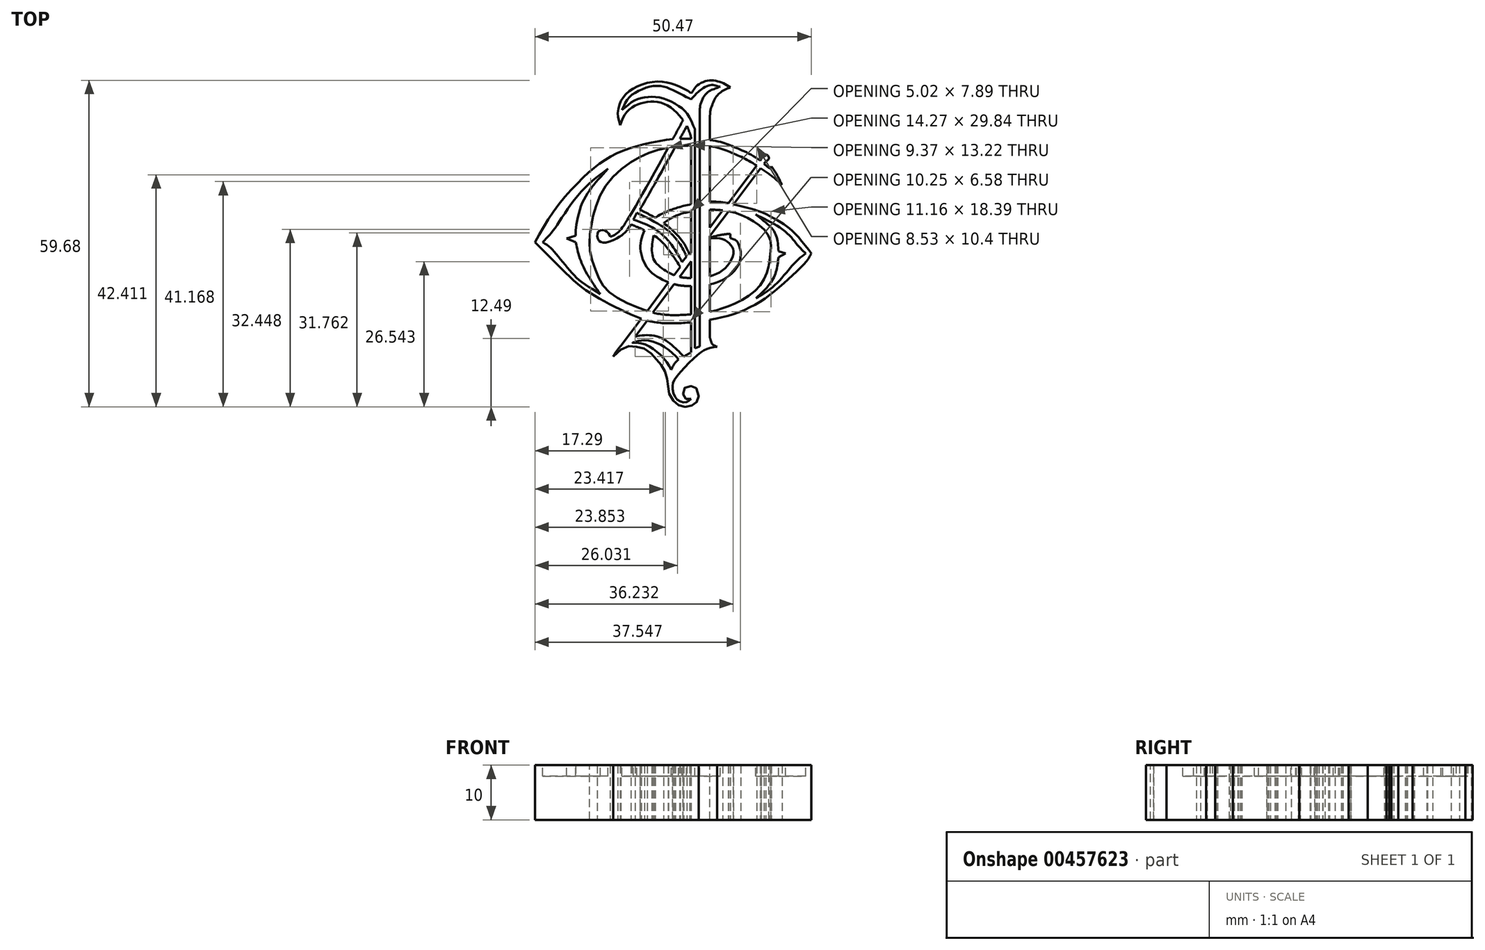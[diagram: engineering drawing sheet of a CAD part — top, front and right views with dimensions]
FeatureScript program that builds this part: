
annotation { "Feature Type Name" : "Feature", "Feature Type Description" : "" }
export const myFeature = defineFeature(function(context is Context, id is Id, definition is map)
    precondition{}
    {
        {
            var Q0;
            Q0=qCreatedBy(makeId("Top.planeOp"),FACE);
            var sketch = newSketch(context, id + "F0", { "sketchPlane" : qUnion([Q0])});
            skFitSpline(sketch, "E0", {"points": [v(7.19, 28.3) * mm, v(5.2, 29.3) * mm, v(2.98, 29.53) * mm, v(0.86, 28.4) * mm, v(0, 27.22) * mm], "startDerivative": vector(-7.6, 5.06) * mm, "endDerivative": vector(-5.78, -5.6) * mm});
            skFitSpline(sketch, "E1", {"points": [v(0, 27.22) * mm, v(-2.3, 28.5) * mm, v(-4.88, 29.3) * mm, v(-8.25, 29.05) * mm, v(-11.21, 27.67) * mm, v(-12.8, 25.88) * mm, v(-13.4, 23.56) * mm, v(-13, 21.39) * mm], "startDerivative": vector(-12.21, 10.9) * mm, "endDerivative": vector(4.4, -17.8) * mm});
            skFitSpline(sketch, "E2", {"points": [v(-13, 21.39) * mm, v(-11.51, 24.1) * mm, v(-9.24, 25.34) * mm, v(-6.86, 25.69) * mm, v(-4.1, 24.85) * mm, v(-1.78, 22.73) * mm, v(-0.84, 21.39) * mm, v(0, 18.97) * mm], "startDerivative": vector(7.24, 20.97) * mm, "endDerivative": vector(2.91, -17.7) * mm});
            skFitSpline(sketch, "E3", {"points": [v(7.19, 28.3) * mm, v(5.8, 27.67) * mm, v(4.62, 26.68) * mm, v(3.88, 25.17) * mm, v(3.43, 23.07) * mm], "startDerivative": vector(-5.92, -2.4) * mm, "endDerivative": vector(0.03, -10.5) * mm});
            skLineSegment(sketch, "E4", {"start": v(3.43, 23.07) * mm, "end": v(3.43, -17.47) * mm});
            skFitSpline(sketch, "E5", {"points": [v(3.43, -17.47) * mm, v(3.87, -18.63) * mm, v(4.71, -19.1) * mm], "startDerivative": vector(0.7, -1.95) * mm, "endDerivative": vector(1.88, -0.91) * mm});
            skFitSpline(sketch, "E6", {"points": [v(4.71, -19.1) * mm, v(2.88, -19.5) * mm, v(0.8, -20.94) * mm, v(-2.86, -24.85) * mm, v(-3.4, -26.53) * mm, v(-2.66, -28.66) * mm, v(-1.08, -29.25) * mm, v(0, -28.66) * mm], "startDerivative": vector(-14.5, -2.01) * mm, "endDerivative": vector(9.2, 7.53) * mm});
            skFitSpline(sketch, "E7", {"points": [v(0, -28.66) * mm, v(-0.88, -28.66) * mm, v(-1.42, -28.01) * mm, v(-1.27, -26.73) * mm, v(0, -26.33) * mm, v(0.9, -26.68) * mm, v(1.35, -28.66) * mm, v(0.74, -29.46) * mm, v(-0.32, -30) * mm, v(-1.87, -30) * mm, v(-3, -29.3) * mm, v(-4.04, -27.62) * mm, v(-4.24, -25.94) * mm, v(-4.64, -24.06) * mm, v(-5.43, -22.47) * mm, v(-6.52, -21.29) * mm, v(-8.1, -19.7) * mm, v(-10.01, -19.1) * mm, v(-11.85, -19.1) * mm, v(-14.23, -20.9) * mm], "startDerivative": vector(-23.72, -3.53) * mm, "endDerivative": vector(-31.28, -31.64) * mm});
            skFitSpline(sketch, "E8", {"points": [v(-14.23, -20.9) * mm, v(-12.7, -18.78) * mm, v(-10.85, -17.47) * mm, v(-8.4, -17) * mm, v(-5.53, -17.47) * mm, v(-3.2, -19.1) * mm, v(-1.37, -20.9) * mm], "startDerivative": vector(8.2, 14.59) * mm, "endDerivative": vector(10.6, -11.27) * mm});
            skFitSpline(sketch, "E9", {"points": [v(-1.37, -20.9) * mm, v(0, -20.12) * mm], "startDerivative": vector(1.37, 0.76) * mm, "endDerivative": vector(1.37, 0.76) * mm});
            skLineSegment(sketch, "E10", {"start": v(0, -20.12) * mm, "end": v(0, 18.97) * mm});
            skSolve(sketch);
        }
        {
            var Q0;
            Q0 = qSketchRegion(id + "F0", true);
            extrude(context, id + "F1", {"entities" : qUnion([Q0]), "depth" : 10 * mm});
        }
        {
            var Q0;
            Q0=qCreatedBy(makeId("Top.planeOp"),FACE);
            var sketch = newSketch(context, id + "F2", { "sketchPlane" : qUnion([Q0])});
            skFitSpline(sketch, "E11", {"points": [v(-28.54, 0) * mm, v(-24.98, 5.83) * mm, v(-20.3, 11.24) * mm, v(-16.87, 14.25) * mm, v(-13.61, 16.22) * mm, v(-9.74, 17.63) * mm, v(-4.7, 18.67) * mm, v(-0.9, 18.92) * mm, v(5.12, 18.37) * mm, v(8.01, 17.32) * mm, v(11.88, 15.42) * mm, v(14.34, 13.51) * mm, v(14.4, 13.51) * mm], "startDerivative": vector(29.87, 53.73) * mm, "endDerivative": vector(4.28, 1.82) * mm});
            skFitSpline(sketch, "E12", {"points": [v(14.4, 13.51) * mm, v(14.65, 13.85) * mm], "startDerivative": vector(0.25, 0.34) * mm, "endDerivative": vector(0.25, 0.34) * mm});
            skFitSpline(sketch, "E13", {"points": [v(14.65, 13.85) * mm, v(15.52, 12.6) * mm, v(16.6, 10.45) * mm], "startDerivative": vector(1.97, -2.6) * mm, "endDerivative": vector(1.92, -4.14) * mm});
            skFitSpline(sketch, "E14", {"points": [v(16.6, 10.45) * mm, v(14.85, 12) * mm, v(12.7, 13.51) * mm, v(10.05, 15.14) * mm, v(7.55, 16.28) * mm, v(4.8, 17.29) * mm, v(-0.9, 17.66) * mm, v(-6.16, 16.82) * mm, v(-10.5, 14.95) * mm, v(-15.12, 10.97) * mm, v(-17.63, 5.83) * mm, v(-18.47, 1.53) * mm, v(-18.47, -1.62) * mm, v(-17.12, -5.96) * mm, v(-15.21, -8.95) * mm, v(-10.75, -11.53) * mm, v(-5.97, -13.09) * mm, v(-1.43, -13.29) * mm, v(3.67, -12.69) * mm, v(6.86, -11.65) * mm, v(11, -9.46) * mm, v(13.7, -5.96) * mm, v(14.4, -2.73) * mm, v(14.4, 0.61) * mm, v(12.2, 3.28) * mm, v(8.89, 5.08) * mm, v(5.18, 5.87) * mm, v(1.52, 5.83) * mm, v(-1.63, 5.24) * mm, v(-4.18, 4.08) * mm, v(-6.6, 1.7) * mm, v(-7.16, -0.98) * mm, v(-6.77, -3.29) * mm, v(-4.7, -5.2) * mm, v(-1.95, -6.4) * mm, v(1.12, -6.48) * mm, v(3.91, -6.08) * mm, v(6.62, -4.32) * mm, v(7.73, -1.82) * mm, v(7.3, -0.58) * mm, v(6.06, 0.42) * mm, v(4.07, 0.77) * mm, v(3.03, 0.73) * mm], "startDerivative": vector(-86.2, 80.4) * mm, "endDerivative": vector(-70.88, -5.73) * mm});
            skFitSpline(sketch, "E15", {"points": [v(3.03, 0.73) * mm, v(5.66, 1.37) * mm, v(7.18, 1.53) * mm], "startDerivative": vector(4.9, 1.33) * mm, "endDerivative": vector(3.3, 0.21) * mm});
            skFitSpline(sketch, "E16", {"points": [v(7.18, 1.53) * mm, v(7.18, 0.77) * mm], "startDerivative": vector(0, -0.76) * mm, "endDerivative": vector(0, -0.76) * mm});
            skFitSpline(sketch, "E17", {"points": [v(7.18, 0.77) * mm, v(7.44, 0.64) * mm, v(8.23, 0.31) * mm, v(8.8, -0.75) * mm, v(9.06, -2.06) * mm, v(8.8, -3.74) * mm, v(8.08, -5.01) * mm, v(6.4, -6.51) * mm, v(4.32, -7.49) * mm, v(2.15, -7.88) * mm, v(-0.57, -8) * mm, v(-3.1, -7.68) * mm, v(-6.5, -6.12) * mm, v(-8.4, -4.05) * mm, v(-9.26, -1.26) * mm, v(-8.87, 1.28) * mm, v(-7.27, 3.9) * mm, v(-4.12, 5.74) * mm, v(-1.12, 6.7) * mm, v(4.26, 7.4) * mm, v(9.22, 6.56) * mm, v(13.17, 5.35) * mm, v(16.8, 3.39) * mm, v(19.25, 1.28) * mm, v(21.93, -2.09) * mm, v(21.8, -2.03) * mm], "startDerivative": vector(15.94, -9.53) * mm, "endDerivative": vector(-19.1, 12.75) * mm});
            skFitSpline(sketch, "E18", {"points": [v(21.93, -2.09) * mm, v(21.15, -3.36) * mm, v(18.22, -6.33) * mm, v(13.42, -10.33) * mm, v(8.18, -12.99) * mm, v(2.11, -14.4) * mm, v(-2.67, -14.81) * mm, v(-7.16, -14.53) * mm, v(-11.78, -12.86) * mm, v(-16.76, -10.3) * mm, v(-20.44, -7.86) * mm, v(-24.05, -4.5) * mm, v(-28.54, 0) * mm], "startDerivative": vector(-13.28, -25.54) * mm, "endDerivative": vector(-48.4, 48) * mm});
            skSolve(sketch);
        }
        {
            var Q0;
            Q0 = qSketchRegion(id + "F2", true);
            extrude(context, id + "F3", {"entities" : qUnion([Q0]), "operationType" : NewBodyOperationType.ADD, "depth" : 10 * mm});
        }
        {
            var Q0;
            Q0=qCreatedBy(makeId("Top.planeOp"),FACE);
            var sketch = newSketch(context, id + "F4", { "sketchPlane" : qUnion([Q0])});
            skFitSpline(sketch, "E19", {"points": [v(0.76, 24.02) * mm, v(-11.9, 1.96) * mm, v(-12.5, 1.42) * mm, v(-13.29, 0.87) * mm, v(-15.26, 0) * mm, v(-16.45, 0) * mm, v(-16.95, 0.43) * mm, v(-17.14, 1.37) * mm, v(-16.85, 2.06) * mm, v(-16.06, 2.2) * mm, v(-15.46, 1.96) * mm, v(-14.87, 1.27) * mm, v(-14.82, 1.02) * mm], "startDerivative": vector(-50.67, -91.69) * mm, "endDerivative": vector(0.03, -6.57) * mm});
            skFitSpline(sketch, "E20", {"points": [v(-14.82, 1.02) * mm, v(-13.9, 1.35) * mm, v(-13.1, 2.08) * mm, v(-11.88, 3.68) * mm, v(-0.55, 24.02) * mm], "startDerivative": vector(7.95, 2.02) * mm, "endDerivative": vector(24.26, 44.74) * mm});
            skFitSpline(sketch, "E21", {"points": [v(-0.55, 24.02) * mm, v(0.76, 24.02) * mm], "startDerivative": vector(1.31, 0) * mm, "endDerivative": vector(1.31, 0) * mm});
            skSolve(sketch);
        }
        {
            var Q0;
            Q0 = qSketchRegion(id + "F4", true);
            extrude(context, id + "F5", {"entities" : qUnion([Q0]), "operationType" : NewBodyOperationType.ADD, "depth" : 10 * mm});
        }
        {
            var Q0;
            Q0=qCreatedBy(makeId("Top.planeOp"),FACE);
            var sketch = newSketch(context, id + "F6", { "sketchPlane" : qUnion([Q0])});
            skLineSegment(sketch, "E22", {"start": v(-13, -19.13) * mm, "end": v(12.84, 15.18) * mm});
            skFitSpline(sketch, "E23", {"points": [v(12.84, 15.18) * mm, v(12.84, 15.59) * mm, v(13.1, 15.94) * mm, v(13.74, 16) * mm, v(14.18, 15.6) * mm, v(14.16, 15.18) * mm, v(13.6, 14.78) * mm], "startDerivative": vector(-0.3, 2.3) * mm, "endDerivative": vector(-3.54, -1) * mm});
            skLineSegment(sketch, "E24", {"start": v(13.6, 14.78) * mm, "end": v(-11.38, -18.79) * mm});
            skLineSegment(sketch, "E25", {"start": v(-13, -19.13) * mm, "end": v(-11.38, -18.79) * mm});
            skSolve(sketch);
        }
        {
            var Q0;
            Q0 = qSketchRegion(id + "F6", true);
            extrude(context, id + "F7", {"entities" : qUnion([Q0]), "operationType" : NewBodyOperationType.ADD, "depth" : 10 * mm});
        }
        {
            var Q0;
            Q0=qCreatedBy(makeId("Top.planeOp"),FACE);
            var sketch = newSketch(context, id + "F8", { "sketchPlane" : qUnion([Q0])});
            skFitSpline(sketch, "E26", {"points": [v(-9.83, 6.17) * mm, v(-7.9, 5.2) * mm, v(-4.12, 2.8) * mm, v(-1.23, -0.37) * mm, v(-0.2, -2.57) * mm], "startDerivative": vector(8.52, -4.1) * mm, "endDerivative": vector(3.34, -9.07) * mm});
            skFitSpline(sketch, "E27", {"points": [v(-0.2, -2.57) * mm, v(-1.92, -4.7) * mm], "startDerivative": vector(-1.67, -2.18) * mm, "endDerivative": vector(-1.67, -2.18) * mm});
            skFitSpline(sketch, "E28", {"points": [v(-1.92, -4.7) * mm, v(-3.28, -2.57) * mm, v(-4.95, -0.37) * mm, v(-7.1, 1.42) * mm, v(-9.7, 2.7) * mm, v(-11.37, 3.41) * mm], "startDerivative": vector(-5.98, 11.13) * mm, "endDerivative": vector(-9.17, 3.87) * mm});
            skFitSpline(sketch, "E29", {"points": [v(-11.37, 3.41) * mm, v(-9.83, 6.17) * mm], "startDerivative": vector(1.54, 2.76) * mm, "endDerivative": vector(1.54, 2.76) * mm});
            skSolve(sketch);
        }
        {
            var Q0;
            Q0 = qSketchRegion(id + "F8", true);
            extrude(context, id + "F9", {"entities" : qUnion([Q0]), "operationType" : NewBodyOperationType.ADD, "depth" : 10 * mm});
        }
        {
            var Q0;
            Q0=qCreatedBy(makeId("Top.planeOp"),FACE);
            cPlane(context, id + "F10", {"entities" : qUnion([Q0]), "cplaneType" : CPlaneType.OFFSET, "offset" : 10 * mm, "width" : 150 * mm, "height" : 150 * mm});
        }
        {
            var Q0;
            Q0=qCreatedBy(id+"F10.planeOp",FACE);
            var sketch = newSketch(context, id + "F11", { "sketchPlane" : qUnion([Q0])});
            skFitSpline(sketch, "E30", {"points": [v(-12.62, 24.16) * mm, v(-11.51, 26.27) * mm, v(-9.73, 27.6) * mm, v(-7.25, 28.5) * mm, v(-5.18, 28.46) * mm, v(-3.47, 27.87) * mm, v(-1.24, 26.71) * mm, v(0, 26.11) * mm], "startDerivative": vector(5.63, 13.57) * mm, "endDerivative": vector(9.68, -4.5) * mm});
            skFitSpline(sketch, "E31", {"points": [v(0, 26.11) * mm, v(0.83, 27.03) * mm, v(1.71, 27.83) * mm, v(3.4, 28.7) * mm, v(4.53, 28.62) * mm, v(5.3, 28.42) * mm], "startDerivative": vector(4.2, 4.54) * mm, "endDerivative": vector(4.4, -0.4) * mm});
            skFitSpline(sketch, "E32", {"points": [v(5.3, 28.42) * mm, v(4.26, 28.03) * mm, v(2.99, 27.39) * mm, v(1.8, 25.48) * mm, v(1.55, 23.84) * mm], "startDerivative": vector(-4.8, -1.93) * mm, "endDerivative": vector(-0.28, -6.14) * mm});
            skLineSegment(sketch, "E33", {"start": v(1.55, 23.84) * mm, "end": v(1.55, -19.04) * mm});
            skLineSegment(sketch, "E34", {"start": v(1.55, -19.04) * mm, "end": v(0.65, -19.4) * mm});
            skLineSegment(sketch, "E35", {"start": v(0.65, -19.4) * mm, "end": v(0.65, 20.67) * mm});
            skFitSpline(sketch, "E36", {"points": [v(0.65, 20.67) * mm, v(-0.38, 23) * mm, v(-1.67, 24.47) * mm, v(-3.74, 25.7) * mm, v(-5.9, 26.45) * mm, v(-7.72, 26.56) * mm, v(-9.5, 26.25) * mm, v(-10.97, 25.52) * mm, v(-12.62, 24.16) * mm], "startDerivative": vector(-6.05, 13.84) * mm, "endDerivative": vector(-12.68, -8.94) * mm});
            skSolve(sketch);
        }
        {
            var Q0;
            Q0 = qSketchRegion(id + "F11", true);
            extrude(context, id + "F12", {"entities" : qUnion([Q0]), "oppositeDirection" : true, "depth" : 2 * mm});
        }
        {
            var Q0;
            Q0=qCreatedBy(id+"F10.planeOp",FACE);
            var sketch = newSketch(context, id + "F13", { "sketchPlane" : qUnion([Q0])});
            skFitSpline(sketch, "E37", {"points": [v(-15.18, 13.42) * mm, v(-20.28, 9.04) * mm, v(-24.42, 3.27) * mm, v(-25.94, 1.24) * mm, v(-27.13, 0) * mm], "startDerivative": vector(-16.53, -12.17) * mm, "endDerivative": vector(-7.56, -7.44) * mm});
            skFitSpline(sketch, "E38", {"points": [v(-27.13, 0) * mm, v(-25.86, -0.88) * mm, v(-24.58, -2.27) * mm, v(-22.47, -4.82) * mm, v(-20.44, -6.93) * mm, v(-16.61, -9.48) * mm], "startDerivative": vector(8.83, -5.4) * mm, "endDerivative": vector(16.29, -9.92) * mm});
            skFitSpline(sketch, "E39", {"points": [v(-16.61, -9.48) * mm, v(-18.8, -6.17) * mm, v(-20.28, -3.1) * mm, v(-21.08, 0) * mm], "startDerivative": vector(-6.52, 9.37) * mm, "endDerivative": vector(-2.09, 9.87) * mm});
            skFitSpline(sketch, "E40", {"points": [v(-15.18, 13.42) * mm, v(-18.05, 10.16) * mm, v(-20.12, 6.57) * mm, v(-21.08, 2.43) * mm, v(-21.08, 1.2) * mm], "startDerivative": vector(-10.52, -11.33) * mm, "endDerivative": vector(0.47, -6.77) * mm});
            skLineSegment(sketch, "E41", {"start": v(-21.08, 1.2) * mm, "end": v(-22.75, 0.68) * mm});
            skLineSegment(sketch, "E42", {"start": v(-22.75, 0.68) * mm, "end": v(-21.08, 0) * mm});
            skSolve(sketch);
        }
        {
            var Q0;
            Q0 = qSketchRegion(id + "F13", true);
            extrude(context, id + "F14", {"entities" : qUnion([Q0]), "oppositeDirection" : true, "depth" : 2 * mm});
        }
        {
            var Q0;
            Q0=qCreatedBy(id+"F10.planeOp",FACE);
            var sketch = newSketch(context, id + "F15", { "sketchPlane" : qUnion([Q0])});
            skFitSpline(sketch, "E43", {"points": [v(11.77, 5.08) * mm, v(17.1, 2.03) * mm, v(19.53, -0.63) * mm, v(20.95, -2.08) * mm], "startDerivative": vector(10.57, -5.14) * mm, "endDerivative": vector(4.88, -4.5) * mm});
            skFitSpline(sketch, "E44", {"points": [v(20.95, -2.08) * mm, v(19.66, -3.07) * mm, v(17.93, -4.93) * mm, v(15.85, -7.3) * mm, v(13.5, -9.26) * mm, v(11.84, -10.25) * mm], "startDerivative": vector(-7.3, -4.86) * mm, "endDerivative": vector(-8.98, -4.89) * mm});
            skFitSpline(sketch, "E45", {"points": [v(11.84, -10.25) * mm, v(14.6, -7.34) * mm, v(15.59, -5.06) * mm, v(15.97, -2.72) * mm], "startDerivative": vector(8.03, 7.5) * mm, "endDerivative": vector(0.99, 7.89) * mm});
            skFitSpline(sketch, "E46", {"points": [v(11.77, 5.08) * mm, v(14.4, 2.9) * mm, v(15.59, 1.04) * mm, v(15.97, -1.66) * mm], "startDerivative": vector(5.08, -4.15) * mm, "endDerivative": vector(0.74, -8) * mm});
            skLineSegment(sketch, "E47", {"start": v(15.97, -1.66) * mm, "end": v(17.26, -2.08) * mm});
            skLineSegment(sketch, "E48", {"start": v(17.26, -2.08) * mm, "end": v(15.97, -2.72) * mm});
            skSolve(sketch);
        }
        {
            var Q0;
            Q0 = qSketchRegion(id + "F15", true);
            extrude(context, id + "F16", {"entities" : qUnion([Q0]), "oppositeDirection" : true, "depth" : 2 * mm});
        }
        {
            var Q0;
            Q0=qCreatedBy(id+"F10.planeOp",FACE);
            var sketch = newSketch(context, id + "F17", { "sketchPlane" : qUnion([Q0])});
            skFitSpline(sketch, "E49", {"points": [v(-3.62, -23.32) * mm, v(-4.66, -21.67) * mm, v(-6.2, -20.07) * mm, v(-7.8, -18.98) * mm, v(-9.7, -18.4) * mm, v(-10.75, -18.36) * mm, v(-8.97, -17.98) * mm, v(-7.03, -18.16) * mm, v(-5.43, -18.8) * mm, v(-3.62, -20.07) * mm, v(-2.28, -21.39) * mm], "startDerivative": vector(-9.1, 16.3) * mm, "endDerivative": vector(12.5, -13.17) * mm});
            skFitSpline(sketch, "E50", {"points": [v(-2.28, -21.39) * mm, v(-3.1, -22.3) * mm, v(-3.62, -23.32) * mm], "startDerivative": vector(-1.78, -1.7) * mm, "endDerivative": vector(-0.9, -2.17) * mm});
            skSolve(sketch);
        }
        {
            var Q0;
            Q0 = qSketchRegion(id + "F17", true);
            extrude(context, id + "F18", {"entities" : qUnion([Q0]), "oppositeDirection" : true, "depth" : 2 * mm});
        }
        {
            var Q0;
            Q0=qCreatedBy(id+"F10.planeOp",FACE);
            var sketch = newSketch(context, id + "F19", { "sketchPlane" : qUnion([Q0])});
            skFitSpline(sketch, "E51", {"points": [v(-10.55, 4.14) * mm, v(-8.85, 3.5) * mm, v(-6.73, 2.47) * mm, v(-5.08, 1.2) * mm, v(-3.79, -0.22) * mm, v(-2.5, -2.1) * mm, v(-1.64, -3.6) * mm], "startDerivative": vector(10.42, -3.77) * mm, "endDerivative": vector(5.13, -9.4) * mm});
            skFitSpline(sketch, "E52", {"points": [v(-1.64, -3.6) * mm, v(-0.82, -2.6) * mm], "startDerivative": vector(0.83, 1) * mm, "endDerivative": vector(0.83, 1) * mm});
            skFitSpline(sketch, "E53", {"points": [v(-0.82, -2.6) * mm, v(-1.46, -1.36) * mm, v(-2.06, -0.32) * mm, v(-3.37, 1.3) * mm, v(-4.97, 2.7) * mm, v(-7.97, 4.4) * mm, v(-9.93, 5.36) * mm], "startDerivative": vector(-4.85, 9.29) * mm, "endDerivative": vector(-10.42, 4.93) * mm});
            skFitSpline(sketch, "E54", {"points": [v(-9.93, 5.36) * mm, v(-10.55, 4.14) * mm], "startDerivative": vector(-0.62, -1.21) * mm, "endDerivative": vector(-0.62, -1.21) * mm});
            skSolve(sketch);
        }
        {
            var Q0;
            Q0 = qSketchRegion(id + "F19", true);
            extrude(context, id + "F20", {"entities" : qUnion([Q0]), "oppositeDirection" : true, "depth" : 2 * mm});
        }
        {
            var Q0;
            Q0=makeQuery(id+"F12.opExtrude","SWEPT_BODY",BODY,{"disambiguationData":[OSD([sQuery(id+"F11.wireOp",EDGE,"E30"),sQuery(id+"F11.wireOp",EDGE,"E31"),sQuery(id+"F11.wireOp",EDGE,"E32"),sQuery(id+"F11.wireOp",EDGE,"E33"),sQuery(id+"F11.wireOp",EDGE,"E34"),sQuery(id+"F11.wireOp",EDGE,"E35"),sQuery(id+"F11.wireOp",EDGE,"E36")])]});
            var Q1;
            Q1=makeQuery(id+"F14.opExtrude","SWEPT_BODY",BODY,{"disambiguationData":[OSD([sQuery(id+"F13.wireOp",EDGE,"E37"),sQuery(id+"F13.wireOp",EDGE,"E38"),sQuery(id+"F13.wireOp",EDGE,"E39"),sQuery(id+"F13.wireOp",EDGE,"E40"),sQuery(id+"F13.wireOp",EDGE,"E41"),sQuery(id+"F13.wireOp",EDGE,"E42")])]});
            var Q2;
            Q2=makeQuery(id+"F16.opExtrude","SWEPT_BODY",BODY,{"disambiguationData":[OSD([sQuery(id+"F15.wireOp",EDGE,"E43"),sQuery(id+"F15.wireOp",EDGE,"E44"),sQuery(id+"F15.wireOp",EDGE,"E45"),sQuery(id+"F15.wireOp",EDGE,"E46"),sQuery(id+"F15.wireOp",EDGE,"E47"),sQuery(id+"F15.wireOp",EDGE,"E48")])]});
            var Q3;
            Q3=makeQuery(id+"F18.opExtrude","SWEPT_BODY",BODY,{"disambiguationData":[OSD([sQuery(id+"F17.wireOp",EDGE,"E49"),sQuery(id+"F17.wireOp",EDGE,"E50")])]});
            var Q4;
            Q4=makeQuery(id+"F20.opExtrude","SWEPT_BODY",BODY,{"disambiguationData":[OSD([sQuery(id+"F19.wireOp",EDGE,"E51"),sQuery(id+"F19.wireOp",EDGE,"E52"),sQuery(id+"F19.wireOp",EDGE,"E53"),sQuery(id+"F19.wireOp",EDGE,"E54")])]});
            var Q5;
            Q5=makeQuery(id+"F1.opExtrude","SWEPT_BODY",BODY,{"disambiguationData":[OSD([sQuery(id+"F0.wireOp",EDGE,"E0"),sQuery(id+"F0.wireOp",EDGE,"E1"),sQuery(id+"F0.wireOp",EDGE,"E2"),sQuery(id+"F0.wireOp",EDGE,"E3"),sQuery(id+"F0.wireOp",EDGE,"E4"),sQuery(id+"F0.wireOp",EDGE,"E5"),sQuery(id+"F0.wireOp",EDGE,"E6"),sQuery(id+"F0.wireOp",EDGE,"E7"),sQuery(id+"F0.wireOp",EDGE,"E8"),sQuery(id+"F0.wireOp",EDGE,"E9"),sQuery(id+"F0.wireOp",EDGE,"E10")])]});
            booleanBodies(context, id + "F21", {"operationType" : BooleanOperationType.SUBTRACTION, "tools" : qUnion([Q0, Q1, Q2, Q3, Q4]), "targets" : qUnion([Q5])});
        }
    });
